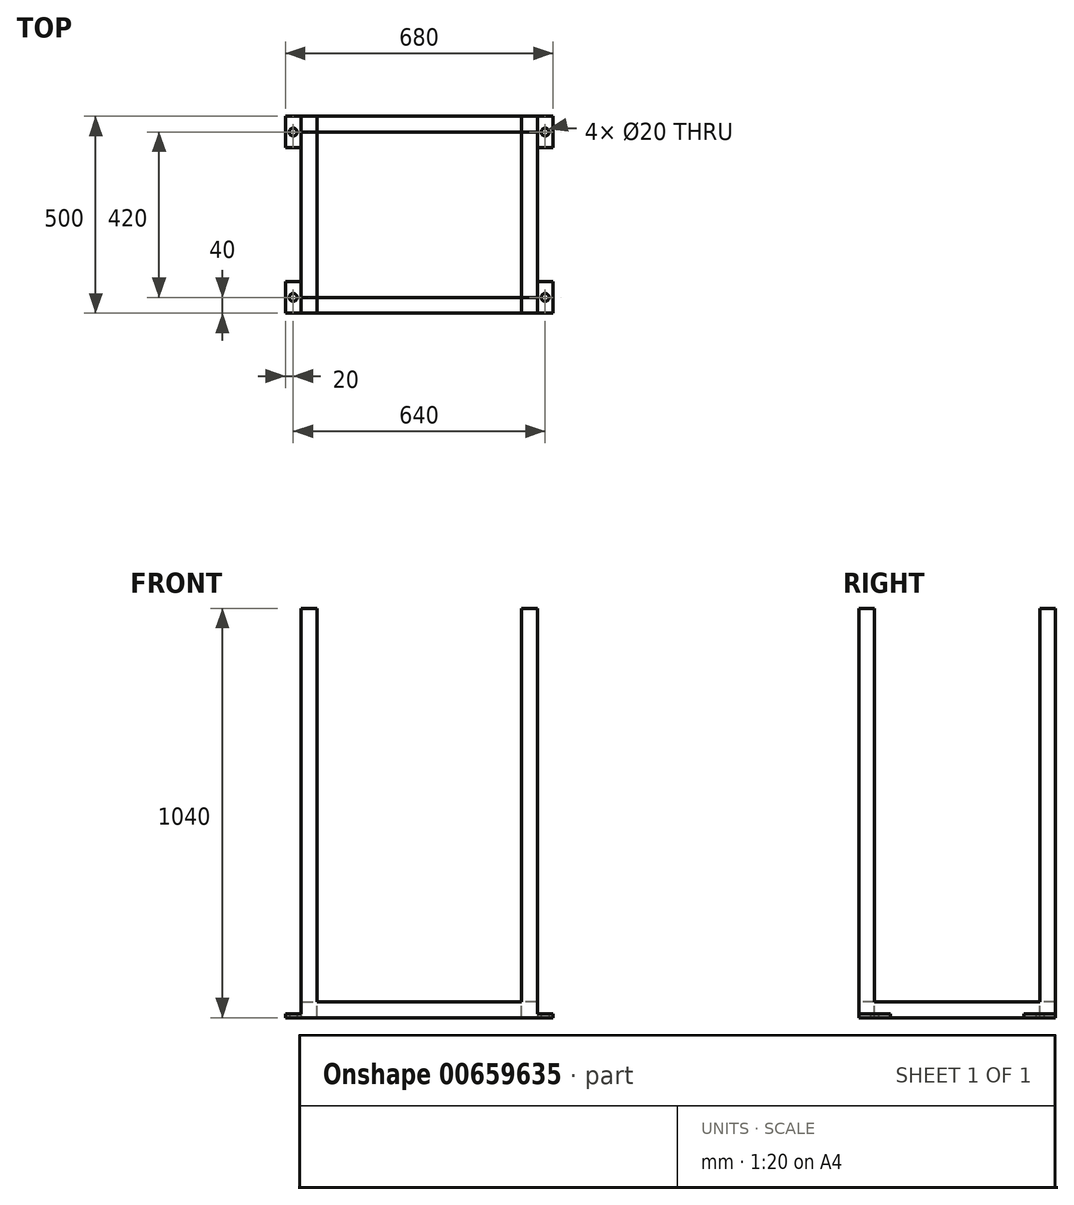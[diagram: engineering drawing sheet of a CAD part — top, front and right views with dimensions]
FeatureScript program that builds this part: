
annotation { "Feature Type Name" : "Feature", "Feature Type Description" : "" }
export const myFeature = defineFeature(function(context is Context, id is Id, definition is map)
    precondition{}
    {
        {
            var Q0;
            Q0=qCreatedBy(makeId("Top.planeOp"),FACE);
            var sketch = newSketch(context, id + "F0", { "sketchPlane" : qUnion([Q0])});
            skLineSegment(sketch, "E0.bottom", {"start": v(300, -250) * mm, "end": v(260, -250) * mm});
            skLineSegment(sketch, "E0.top", {"start": v(300, 250) * mm, "end": v(260, 250) * mm});
            skLineSegment(sketch, "E0.left", {"start": v(300, -250) * mm, "end": v(300, 250) * mm});
            skLineSegment(sketch, "E0.right", {"start": v(-300, -250) * mm, "end": v(-300, 250) * mm});
            skPoint(sketch, "E0.middle", {"position": v(0, 0) * mm});
            skLineSegment(sketch, "E1", {"start": v(-260, 250) * mm, "end": v(-260, -250) * mm});
            skLineSegment(sketch, "E2", {"start": v(260, 250) * mm, "end": v(260, -250) * mm});
            skLineSegment(sketch, "E3.trimOffspring", {"start": v(-260, 250) * mm, "end": v(-300, 250) * mm});
            skLineSegment(sketch, "E4.trimOffspring", {"start": v(-260, -250) * mm, "end": v(-300, -250) * mm});
            skSolve(sketch);
        }
        {
            var Q0;
            Q0=qSketchRegion(id+"F0",true);
            extrude(context, id + "F1", {"entities" : qUnion([Q0]), "oppositeDirection" : true, "depth" : 40 * mm, "offsetDistance" : 25 * mm});
        }
        {
            var Q0;
            Q0=makeQuery(id+"F1.opExtrude","CAP_FACE",FACE,{"disambiguationData":[OSD([sQuery(id+"F0.wireOp",EDGE,"E0.bottom"),sQuery(id+"F0.wireOp",EDGE,"E0.top"),sQuery(id+"F0.wireOp",EDGE,"E0.left"),sQuery(id+"F0.wireOp",EDGE,"E0.right"),sQuery(id+"F0.wireOp",EDGE,"NNcdynhF-evRW-wMSb-w858-wxC3enGbxYDO.bottom"),sQuery(id+"F0.wireOp",EDGE,"NNcdynhF-evRW-wMSb-w858-wxC3enGbxYDO.top"),sQuery(id+"F0.wireOp",EDGE,"NNcdynhF-evRW-wMSb-w858-wxC3enGbxYDO.left"),sQuery(id+"F0.wireOp",EDGE,"NNcdynhF-evRW-wMSb-w858-wxC3enGbxYDO.right")])],"isStart":false});
            var sketch = newSketch(context, id + "F2", { "sketchPlane" : qUnion([Q0])});
            skLineSegment(sketch, "E5.bottom", {"start": v(300, -250) * mm, "end": v(260, -250) * mm});
            skLineSegment(sketch, "E5.top", {"start": v(300, -210) * mm, "end": v(260, -210) * mm});
            skLineSegment(sketch, "E5.left", {"start": v(300, -250) * mm, "end": v(300, -210) * mm});
            skLineSegment(sketch, "E5.right", {"start": v(260, -250) * mm, "end": v(260, -210) * mm});
            skLineSegment(sketch, "E6.MirrorCS", {"start": v(-260, -250) * mm, "end": v(-260, -210) * mm});
            skLineSegment(sketch, "E7.MirrorCS", {"start": v(-300, -250) * mm, "end": v(-300, -210) * mm});
            skLineSegment(sketch, "E8.MirrorCS", {"start": v(-300, -210) * mm, "end": v(-260, -210) * mm});
            skLineSegment(sketch, "E9.MirrorCS", {"start": v(-300, -250) * mm, "end": v(-260, -250) * mm});
            skLineSegment(sketch, "E10.MirrorCS", {"start": v(300, 250) * mm, "end": v(300, 210) * mm});
            skLineSegment(sketch, "E11.MirrorCS", {"start": v(300, 210) * mm, "end": v(260, 210) * mm});
            skLineSegment(sketch, "E12.MirrorCS", {"start": v(300, 250) * mm, "end": v(260, 250) * mm});
            skLineSegment(sketch, "E13.MirrorCS", {"start": v(-300, 250) * mm, "end": v(-260, 250) * mm});
            skLineSegment(sketch, "E14.MirrorCS", {"start": v(-300, 210) * mm, "end": v(-260, 210) * mm});
            skLineSegment(sketch, "E15.MirrorCS", {"start": v(-260, 250) * mm, "end": v(-260, 210) * mm});
            skLineSegment(sketch, "E16.MirrorCS", {"start": v(-300, 250) * mm, "end": v(-300, 210) * mm});
            skLineSegment(sketch, "E17.MirrorCS", {"start": v(260, 250) * mm, "end": v(260, 210) * mm});
            skSolve(sketch);
        }
        {
            var Q0;
            Q0=qSketchRegion(id+"F2",true);
            extrude(context, id + "F3", {"entities" : qUnion([Q0]), "operationType" : NewBodyOperationType.ADD, "depth" : 1000 * mm, "offsetDistance" : 25 * mm});
        }
        {
            var Q0;
            Q0=makeQuery(id+"F3.opExtrude","CAP_FACE",FACE,{"disambiguationData":[OSD([sQuery(id+"F2.wireOp",EDGE,"E10.MirrorCS"),sQuery(id+"F2.wireOp",EDGE,"E11.MirrorCS"),sQuery(id+"F2.wireOp",EDGE,"E12.MirrorCS"),sQuery(id+"F2.wireOp",EDGE,"E17.MirrorCS")])],"isStart":false});
            var sketch = newSketch(context, id + "F4", { "sketchPlane" : qUnion([Q0])});
            skLineSegment(sketch, "E18.bottom", {"start": v(-300, 250) * mm, "end": v(300, 250) * mm});
            skLineSegment(sketch, "E18.top", {"start": v(-300, -250) * mm, "end": v(300, -250) * mm});
            skLineSegment(sketch, "E18.left", {"start": v(-300, 250) * mm, "end": v(-300, -250) * mm});
            skLineSegment(sketch, "E18.right", {"start": v(300, 250) * mm, "end": v(300, -250) * mm});
            skLineSegment(sketch, "E19.bottom", {"start": v(-260, 210) * mm, "end": v(260, 210) * mm});
            skLineSegment(sketch, "E19.top", {"start": v(-260, -210) * mm, "end": v(260, -210) * mm});
            skLineSegment(sketch, "E19.left", {"start": v(-260, 210) * mm, "end": v(-260, -210) * mm});
            skLineSegment(sketch, "E19.right", {"start": v(260, 210) * mm, "end": v(260, -210) * mm});
            skSolve(sketch);
        }
        {
            var Q0;
            Q0 = qSketchRegion(id + "F4", true);
            extrude(context, id + "F5", {"entities" : qUnion([Q0]), "operationType" : NewBodyOperationType.ADD, "depth" : 40 * mm, "offsetDistance" : 25 * mm});
        }
        {
            var Q0;
            Q0=makeQuery(id+"F5.opExtrude","CAP_FACE",FACE,{"disambiguationData":[OSD([sQuery(id+"F4.wireOp",EDGE,"E18.bottom"),sQuery(id+"F4.wireOp",EDGE,"E18.top"),sQuery(id+"F4.wireOp",EDGE,"E18.left"),sQuery(id+"F4.wireOp",EDGE,"E18.right"),sQuery(id+"F4.wireOp",EDGE,"E19.bottom"),sQuery(id+"F4.wireOp",EDGE,"E19.top"),sQuery(id+"F4.wireOp",EDGE,"E19.left"),sQuery(id+"F4.wireOp",EDGE,"E19.right")])],"isStart":false});
            var sketch = newSketch(context, id + "F6", { "sketchPlane" : qUnion([Q0])});
            skLineSegment(sketch, "E20.bottom", {"start": v(-300, 250) * mm, "end": v(-340, 250) * mm});
            skLineSegment(sketch, "E20.top", {"start": v(-300, 170) * mm, "end": v(-340, 170) * mm});
            skLineSegment(sketch, "E20.left", {"start": v(-300, 250) * mm, "end": v(-300, 170) * mm});
            skLineSegment(sketch, "E20.right", {"start": v(-340, 250) * mm, "end": v(-340, 170) * mm});
            skCircle(sketch, "E21", {"center": v(-320, 210) * mm, "radius": 10 * mm});
            skLineSegment(sketch, "E22.MirrorCS", {"start": v(300, 170) * mm, "end": v(340, 170) * mm});
            skLineSegment(sketch, "E23.MirrorCS", {"start": v(300, 250) * mm, "end": v(300, 170) * mm});
            skLineSegment(sketch, "E24.MirrorCS", {"start": v(300, 250) * mm, "end": v(340, 250) * mm});
            skLineSegment(sketch, "E25.MirrorCS", {"start": v(340, 250) * mm, "end": v(340, 170) * mm});
            skCircle(sketch, "E26.MirrorC", {"center": v(320, 210) * mm, "radius": 10 * mm});
            skLineSegment(sketch, "E27.MirrorCS", {"start": v(-300, -250) * mm, "end": v(-340, -250) * mm});
            skLineSegment(sketch, "E28.MirrorCS", {"start": v(300, -250) * mm, "end": v(340, -250) * mm});
            skLineSegment(sketch, "E29.MirrorCS", {"start": v(-340, -250) * mm, "end": v(-340, -170) * mm});
            skLineSegment(sketch, "E30.MirrorCS", {"start": v(300, -170) * mm, "end": v(340, -170) * mm});
            skLineSegment(sketch, "E31.MirrorCS", {"start": v(300, -250) * mm, "end": v(300, -170) * mm});
            skLineSegment(sketch, "E32.MirrorCS", {"start": v(340, -250) * mm, "end": v(340, -170) * mm});
            skLineSegment(sketch, "E33.MirrorCS", {"start": v(-300, -170) * mm, "end": v(-340, -170) * mm});
            skCircle(sketch, "E34.MirrorC", {"center": v(-320, -210) * mm, "radius": 10 * mm});
            skCircle(sketch, "E35.MirrorC", {"center": v(320, -210) * mm, "radius": 10 * mm});
            skLineSegment(sketch, "E36.MirrorCS", {"start": v(-300, -250) * mm, "end": v(-300, -170) * mm});
            skSolve(sketch);
        }
        {
            var Q0;
            Q0 = qSketchRegion(id + "F6", true);
            extrude(context, id + "F7", {"entities" : qUnion([Q0]), "operationType" : NewBodyOperationType.ADD, "oppositeDirection" : true, "depth" : 10 * mm, "offsetDistance" : 25 * mm});
        }
        {
            var Q0;
            Q0=makeQuery(id+"F1.opExtrude","CAP_FACE",FACE,{"disambiguationData":[OSD([sQuery(id+"F0.wireOp",EDGE,"E0.right"),sQuery(id+"F0.wireOp",EDGE,"E1"),sQuery(id+"F0.wireOp",EDGE,"E3.trimOffspring"),sQuery(id+"F0.wireOp",EDGE,"E4.trimOffspring")])],"isStart":true});
            var sketch = newSketch(context, id + "F8", { "sketchPlane" : qUnion([Q0])});
            skLineSegment(sketch, "E37.bottom", {"start": v(-300, 250) * mm, "end": v(300, 250) * mm});
            skLineSegment(sketch, "E37.top", {"start": v(-300, -250) * mm, "end": v(300, -250) * mm});
            skLineSegment(sketch, "E37.left", {"start": v(-300, 250) * mm, "end": v(-300, -250) * mm});
            skLineSegment(sketch, "E37.right", {"start": v(300, 250) * mm, "end": v(300, -250) * mm});
            skSolve(sketch);
        }
        {
            var Q0;
            Q0 = qSketchRegion(id + "F8", true);
            extrude(context, id + "F9", {"entities" : qUnion([Q0]), "operationType" : NewBodyOperationType.REMOVE, "oppositeDirection" : true, "depth" : 40 * mm, "offsetDistance" : 25 * mm});
        }
    });
